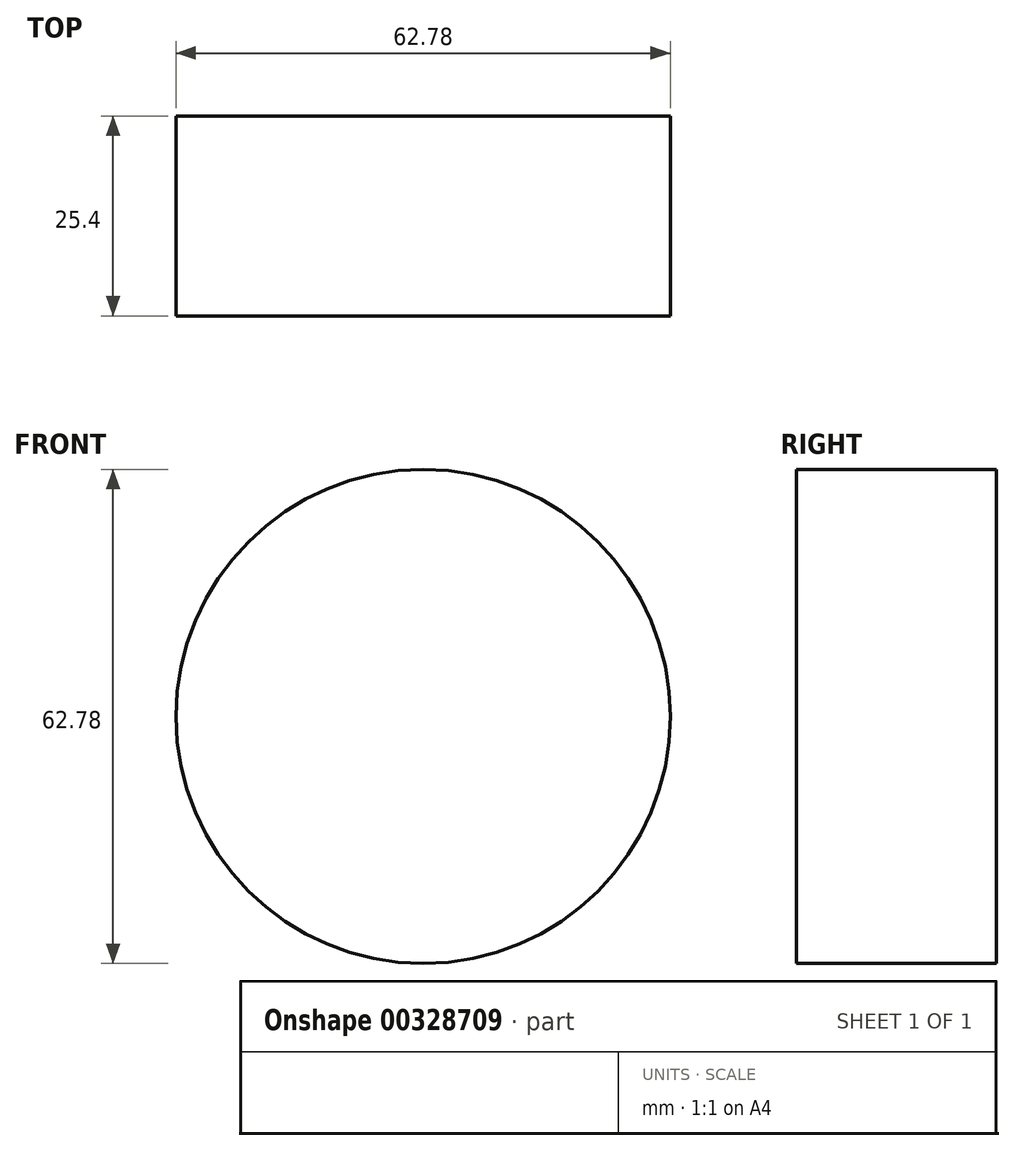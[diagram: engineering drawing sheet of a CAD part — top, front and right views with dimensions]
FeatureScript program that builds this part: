
annotation { "Feature Type Name" : "Feature", "Feature Type Description" : "" }
export const myFeature = defineFeature(function(context is Context, id is Id, definition is map)
    precondition{}
    {
        {
            var Q0;
            Q0=qCreatedBy(makeId("Front.planeOp"),FACE);
            var sketch = newSketch(context, id + "F0", { "sketchPlane" : qUnion([Q0])});
            skCircle(sketch, "E0", {"center": v(0, 0) * mm, "radius": 31.39 * mm});
            skSolve(sketch);
        }
        {
            var Q0;
            Q0=makeQuery(id+"F0.imprint","IMPRINT",FACE,{"disambiguationData":[TD([[makeQuery(id+"F0.imprint","IMPRINT",EDGE,{"derivedFrom":sQuery(id+"F0.wireOp",EDGE,"E0")}),1.0]])]});
            extrude(context, id + "F1", {"entities" : qUnion([Q0]), "depth" : 25.4 * mm});
        }
    });
